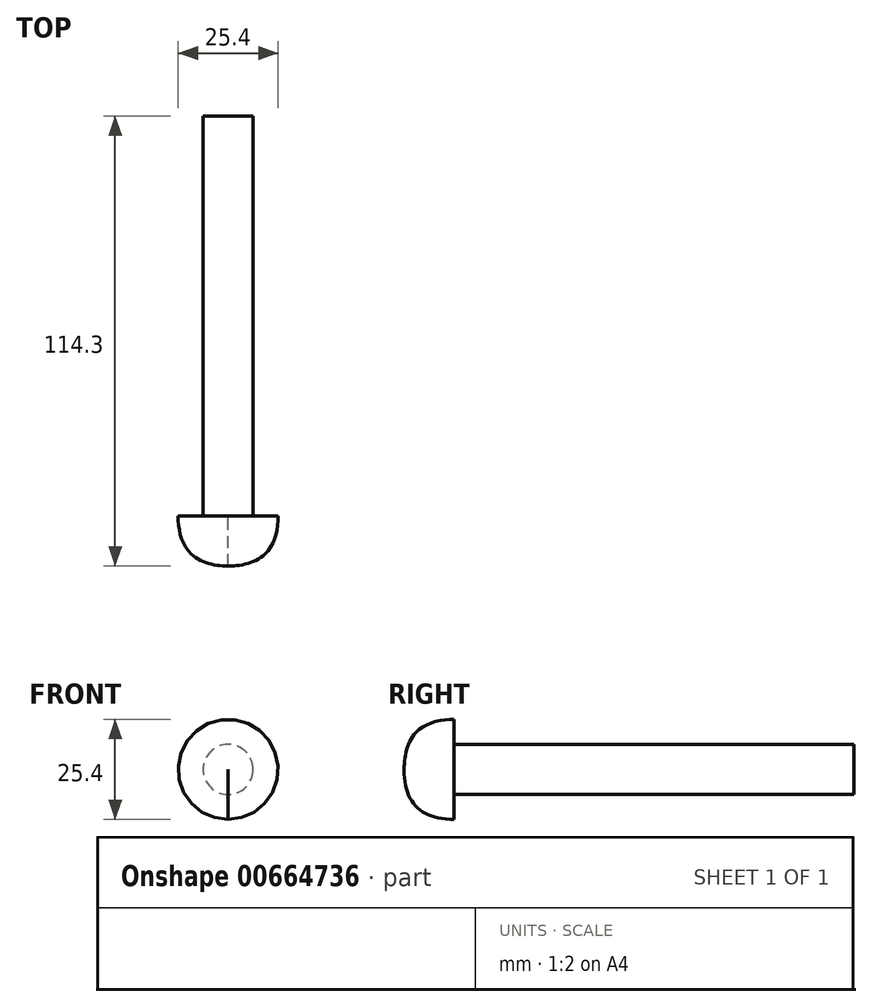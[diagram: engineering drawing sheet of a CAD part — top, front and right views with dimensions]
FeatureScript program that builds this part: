
annotation { "Feature Type Name" : "Feature", "Feature Type Description" : "" }
export const myFeature = defineFeature(function(context is Context, id is Id, definition is map)
    precondition{}
    {
        {
            var Q0;
            Q0=qCreatedBy(makeId("Front.planeOp"),FACE);
            var sketch = newSketch(context, id + "F0", { "sketchPlane" : qUnion([Q0])});
            skCircle(sketch, "E0", {"center": v(0, 0) * mm, "radius": 6.35 * mm});
            skSolve(sketch);
        }
        {
            var Q0;
            Q0=makeQuery(id+"F0.imprint","IMPRINT",FACE,{"disambiguationData":[TD([[makeQuery(id+"F0.imprint","IMPRINT",EDGE,{"derivedFrom":sQuery(id+"F0.wireOp",EDGE,"E0")}),1.0]])]});
            extrude(context, id + "F1", {"entities" : qUnion([Q0]), "oppositeDirection" : true, "depth" : 101.6 * mm, "offsetDistance" : 25.4 * mm});
        }
        {
            var Q0;
            Q0=makeQuery(id+"F1.opExtrude","CAP_FACE",FACE,{"disambiguationData":[OSD([sQuery(id+"F0.wireOp",EDGE,"E0")])],"isStart":true});
            var sketch = newSketch(context, id + "F2", { "sketchPlane" : qUnion([Q0])});
            skCircle(sketch, "E1", {"center": v(0, 0) * mm, "radius": 12.7 * mm});
            skSolve(sketch);
        }
        {
            var Q0;
            Q0 = qSketchRegion(id + "F2", true);
            var Q1;
            Q1 = qSketchRegion(id + "F0", true);
            extrude(context, id + "F3", {"entities" : qUnion([Q0, Q1]), "operationType" : NewBodyOperationType.ADD, "depth" : 12.7 * mm, "offsetDistance" : 25.4 * mm});
        }
        {
            var Q0;
            Q0=makeQuery(id+"F3.opExtrude","CAP_EDGE",EDGE,{"disambiguationData":[OSD([sQuery(id+"F2.wireOp",EDGE,"E1")])],"isStart":false});
            fillet(context, id + "F4", {"entities" : qUnion([Q0]), "radius" : 12.7 * mm, "tangentPropagation" : true, "rho" : 0.5, "crossSection" : FilletCrossSection.CONIC, "allowEdgeOverflow" : false});
        }
    });
